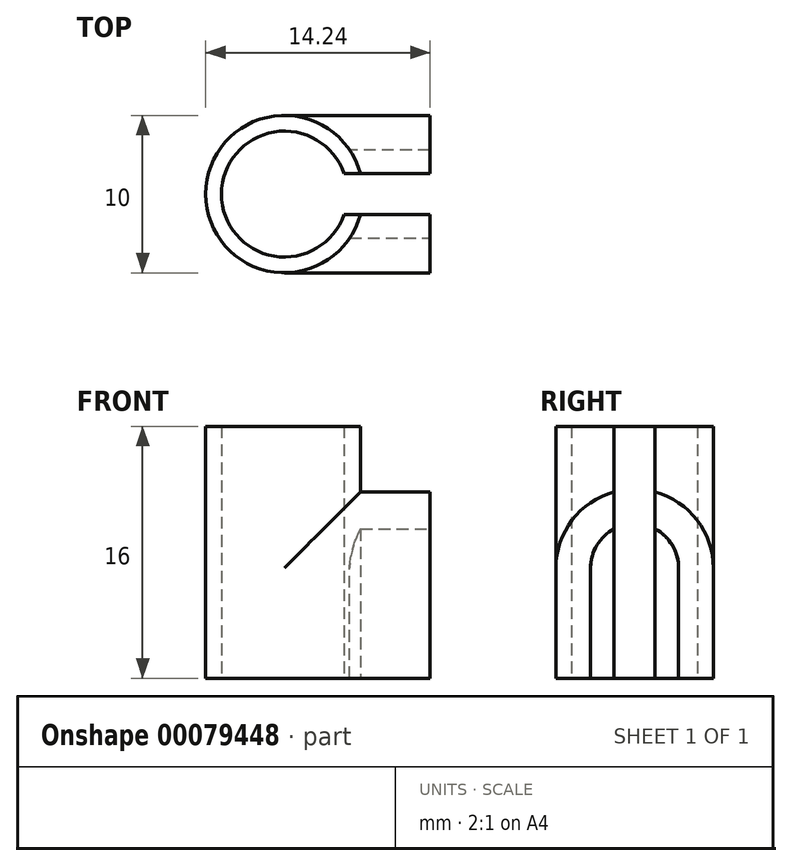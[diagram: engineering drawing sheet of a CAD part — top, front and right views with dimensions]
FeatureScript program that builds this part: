
annotation { "Feature Type Name" : "Feature", "Feature Type Description" : "" }
export const myFeature = defineFeature(function(context is Context, id is Id, definition is map)
    precondition{}
    {
        {
            var Q0;
            Q0=qCreatedBy(makeId("Top.planeOp"),FACE);
            var sketch = newSketch(context, id + "F0", { "sketchPlane" : qUnion([Q0])});
            skCircle(sketch, "E0", {"center": v(-30.88, -8.21) * mm, "radius": 4 * mm});
            skCircle(sketch, "E1", {"center": v(-30.88, -8.21) * mm, "radius": 5 * mm});
            skLineSegment(sketch, "E2", {"start": v(-30.88, -8.21) * mm, "end": v(-21.59, -8.21) * mm});
            skLineSegment(sketch, "E3", {"start": v(-30.88, -3.21) * mm, "end": v(-21.64, -3.21) * mm});
            skLineSegment(sketch, "E4", {"start": v(-21.64, -3.21) * mm, "end": v(-21.64, -5.42) * mm});
            skLineSegment(sketch, "E5", {"start": v(-21.64, -5.42) * mm, "end": v(-28.02, -5.42) * mm});
            skLineSegment(sketch, "E6", {"start": v(-28.02, -11) * mm, "end": v(-21.64, -11) * mm});
            skLineSegment(sketch, "E7", {"start": v(-21.64, -11) * mm, "end": v(-21.64, -13.21) * mm});
            skLineSegment(sketch, "E8", {"start": v(-21.64, -13.21) * mm, "end": v(-30.88, -13.21) * mm});
            skLineSegment(sketch, "E9", {"start": v(-27.1, -6.91) * mm, "end": v(-26.05, -6.91) * mm});
            skLineSegment(sketch, "E10", {"start": v(-27.1, -9.51) * mm, "end": v(-26.05, -9.51) * mm});
            skLineSegment(sketch, "E11", {"start": v(-21.64, -5.42) * mm, "end": v(-21.59, -8.21) * mm});
            skLineSegment(sketch, "E12", {"start": v(-21.59, -8.21) * mm, "end": v(-21.64, -11) * mm});
            skLineSegment(sketch, "E13", {"start": v(-26.05, -6.91) * mm, "end": v(-21.61, -6.91) * mm});
            skLineSegment(sketch, "E14", {"start": v(-26.05, -9.51) * mm, "end": v(-21.61, -9.51) * mm});
            skSolve(sketch);
        }
        {
            var Q0;
            {var subQ4=sQuery(id+"F0.wireOp",EDGE,"E5");var subQ5=sQuery(id+"F0.wireOp",EDGE,"E0");var subQ6=makeQuery(id+"F0.imprint","INTERSECT",VERTEX,{"derivedFrom":[subQ5,subQ4]});Q0=makeQuery(id+"F0.imprint","IMPRINT",FACE,{"disambiguationData":[TD([[makeQuery(id+"F0.imprint","IMPRINT",EDGE,{"disambiguationData":[TD([[subQ6,-1.0]])],"derivedFrom":subQ5}),-1.0]])]});}
            var Q1;
            {var subQ3=sQuery(id+"F0.wireOp",EDGE,"E10");Q1=makeQuery(id+"F0.imprint","IMPRINT",FACE,{"disambiguationData":[TD([[makeQuery(id+"F0.imprint","IMPRINT",EDGE,{"derivedFrom":subQ3}),-1.0]])]});}
            var Q2;
            {var subQ3=sQuery(id+"F0.wireOp",EDGE,"E9");Q2=makeQuery(id+"F0.imprint","IMPRINT",FACE,{"disambiguationData":[TD([[makeQuery(id+"F0.imprint","IMPRINT",EDGE,{"derivedFrom":subQ3}),1.0]])]});}
            extrude(context, id + "F1", {"entities" : qUnion([Q0, Q1, Q2]), "depth" : 9 * mm});
        }
        {
            var Q0;
            {var subQ0=sQuery(id+"F0.wireOp",EDGE,"E3");Q0=makeQuery(id+"F0.imprint","IMPRINT",FACE,{"disambiguationData":[TD([[makeQuery(id+"F0.imprint","IMPRINT",EDGE,{"derivedFrom":subQ0}),-1.0]])]});}
            var Q1;
            {var subQ4=sQuery(id+"F0.wireOp",EDGE,"E5");var subQ5=sQuery(id+"F0.wireOp",EDGE,"E0");var subQ6=makeQuery(id+"F0.imprint","INTERSECT",VERTEX,{"derivedFrom":[subQ5,subQ4]});Q1=makeQuery(id+"F0.imprint","IMPRINT",FACE,{"disambiguationData":[TD([[makeQuery(id+"F0.imprint","IMPRINT",EDGE,{"disambiguationData":[TD([[subQ6,-1.0]])],"derivedFrom":subQ5}),-1.0]])]});}
            var Q2;
            {var subQ4=sQuery(id+"F0.wireOp",EDGE,"E7");Q2=makeQuery(id+"F0.imprint","IMPRINT",FACE,{"disambiguationData":[TD([[makeQuery(id+"F0.imprint","IMPRINT",EDGE,{"derivedFrom":subQ4}),-1.0]])]});}
            var Q3;
            {var subQ3=sQuery(id+"F0.wireOp",EDGE,"E10");Q3=makeQuery(id+"F0.imprint","IMPRINT",FACE,{"disambiguationData":[TD([[makeQuery(id+"F0.imprint","IMPRINT",EDGE,{"derivedFrom":subQ3}),-1.0]])]});}
            var Q4;
            {var subQ3=sQuery(id+"F0.wireOp",EDGE,"E9");Q4=makeQuery(id+"F0.imprint","IMPRINT",FACE,{"disambiguationData":[TD([[makeQuery(id+"F0.imprint","IMPRINT",EDGE,{"derivedFrom":subQ3}),1.0]])]});}
            extrude(context, id + "F2", {"entities" : qUnion([Q0, Q1, Q2, Q3, Q4]), "operationType" : NewBodyOperationType.ADD, "oppositeDirection" : true, "depth" : 7 * mm});
        }
        {
            var Q0;
            {var subQ4=sQuery(id+"F0.wireOp",EDGE,"E7");Q0=makeQuery(id+"F0.imprint","IMPRINT",FACE,{"disambiguationData":[TD([[makeQuery(id+"F0.imprint","IMPRINT",EDGE,{"derivedFrom":subQ4}),-1.0]])]});}
            var Q1;
            Q1=sQuery(id+"F0.wireOp",EDGE,"E2");
            revolve(context, id + "F3", {"operationType" : NewBodyOperationType.ADD, "entities" : qUnion([Q0]), "axis" : qUnion([Q1]), "revolveType" : RevolveType.ONE_DIRECTION, "oppositeDirection" : true, "angle" : 180 * degree});
        }
        {
            var Q0;
            {var subQ0=sQuery(id+"F0.wireOp",EDGE,"E13");Q0=makeQuery(id+"F0.imprint","IMPRINT",FACE,{"disambiguationData":[TD([[makeQuery(id+"F0.imprint","IMPRINT",EDGE,{"derivedFrom":subQ0}),-1.0]])]});}
            var Q1;
            {var subQ0=sQuery(id+"F0.wireOp",EDGE,"E0");var subQ4=makeQuery(id+"F0.imprint","INTERSECT",VERTEX,{"derivedFrom":[subQ0,sQuery(id+"F0.wireOp",EDGE,"E9")]});Q1=makeQuery(id+"F0.imprint","IMPRINT",FACE,{"disambiguationData":[TD([[makeQuery(id+"F0.imprint","IMPRINT",EDGE,{"disambiguationData":[TD([[subQ4,1.0]])],"derivedFrom":subQ0}),1.0]])]});}
            var Q2;
            {var subQ0=sQuery(id+"F0.wireOp",EDGE,"E9");Q2=makeQuery(id+"F0.imprint","IMPRINT",FACE,{"disambiguationData":[TD([[makeQuery(id+"F0.imprint","IMPRINT",EDGE,{"derivedFrom":subQ0}),-1.0]])]});}
            var Q3;
            {var subQ0=sQuery(id+"F0.wireOp",EDGE,"E10");Q3=makeQuery(id+"F0.imprint","IMPRINT",FACE,{"disambiguationData":[TD([[makeQuery(id+"F0.imprint","IMPRINT",EDGE,{"derivedFrom":subQ0}),1.0]])]});}
            var Q4;
            {var subQ0=sQuery(id+"F0.wireOp",EDGE,"E14");Q4=makeQuery(id+"F0.imprint","IMPRINT",FACE,{"disambiguationData":[TD([[makeQuery(id+"F0.imprint","IMPRINT",EDGE,{"derivedFrom":subQ0}),1.0]])]});}
            extrude(context, id + "F4", {"entities" : qUnion([Q0, Q1, Q2, Q3, Q4]), "operationType" : NewBodyOperationType.REMOVE, "endBound" : BoundingType.SYMMETRIC, "oppositeDirection" : true, "depth" : 49.62 * mm});
        }
    });
